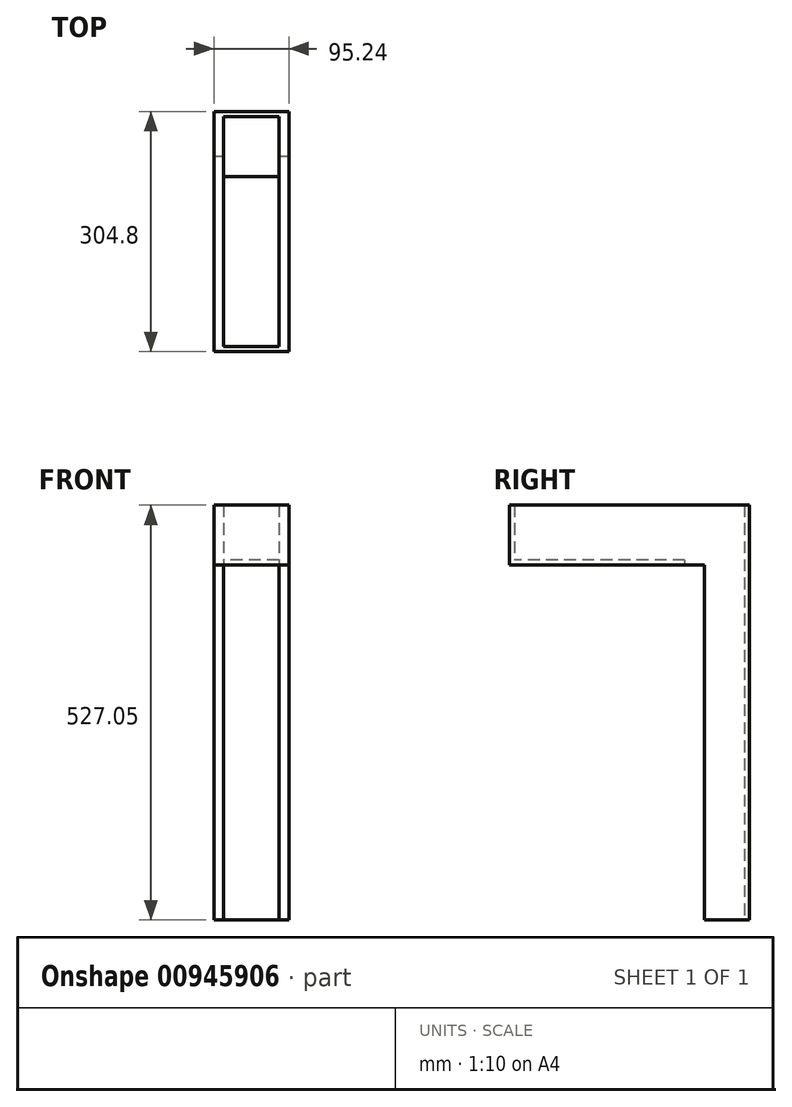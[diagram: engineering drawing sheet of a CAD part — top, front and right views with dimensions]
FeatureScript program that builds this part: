
annotation { "Feature Type Name" : "Feature", "Feature Type Description" : "" }
export const myFeature = defineFeature(function(context is Context, id is Id, definition is map)
    precondition{}
    {
        {
            var Q0;
            Q0=qCreatedBy(makeId("Top.planeOp"),FACE);
            var sketch = newSketch(context, id + "F0", { "sketchPlane" : qUnion([Q0])});
            skLineSegment(sketch, "E0.bottom", {"start": v(47.62, 152.4) * mm, "end": v(-47.63, 152.4) * mm});
            skLineSegment(sketch, "E0.top", {"start": v(47.63, -152.4) * mm, "end": v(-47.62, -152.4) * mm});
            skLineSegment(sketch, "E0.left", {"start": v(47.62, 152.4) * mm, "end": v(47.63, -152.4) * mm});
            skLineSegment(sketch, "E0.right", {"start": v(-47.63, 152.4) * mm, "end": v(-47.62, -152.4) * mm});
            skPoint(sketch, "E0.middle", {"position": v(0, 0) * mm});
            skLineSegment(sketch, "E1.bottom", {"start": v(34.92, 146.05) * mm, "end": v(-34.93, 146.05) * mm});
            skLineSegment(sketch, "E1.top", {"start": v(34.93, -146.05) * mm, "end": v(-34.92, -146.05) * mm});
            skLineSegment(sketch, "E1.left", {"start": v(34.93, 146.05) * mm, "end": v(34.93, -146.05) * mm});
            skLineSegment(sketch, "E1.right", {"start": v(-34.93, 146.05) * mm, "end": v(-34.93, -146.05) * mm});
            skSolve(sketch);
        }
        {
            var Q0;
            Q0=makeQuery(id+"F0.imprint","IMPRINT",FACE,{"disambiguationData":[TD([[makeQuery(id+"F0.imprint","IMPRINT",EDGE,{"derivedFrom":sQuery(id+"F0.wireOp",EDGE,"E0.bottom")}),1.0]])]});
            extrude(context, id + "F1", {"entities" : qUnion([Q0]), "depth" : 69.85 * mm, "offsetDistance" : 25.4 * mm});
        }
        {
            var Q0;
            Q0=makeQuery(id+"F0.imprint","IMPRINT",FACE,{"disambiguationData":[TD([[makeQuery(id+"F0.imprint","IMPRINT",EDGE,{"derivedFrom":sQuery(id+"F0.wireOp",EDGE,"E0.bottom")}),1.0]])]});
            var Q1;
            Q1=makeQuery(id+"F0.imprint","IMPRINT",FACE,{"disambiguationData":[TD([[makeQuery(id+"F0.imprint","IMPRINT",EDGE,{"derivedFrom":sQuery(id+"F0.wireOp",EDGE,"E1.bottom")}),1.0]])]});
            extrude(context, id + "F2", {"entities" : qUnion([Q0, Q1]), "operationType" : NewBodyOperationType.ADD, "oppositeDirection" : true, "depth" : 6.35 * mm, "offsetDistance" : 25.4 * mm});
        }
        {
            var Q0;
            Q0=makeQuery(id+"F2.opExtrude","CAP_FACE",FACE,{"disambiguationData":[OSD([sQuery(id+"F0.wireOp",EDGE,"E0.bottom"),sQuery(id+"F0.wireOp",EDGE,"E0.top"),sQuery(id+"F0.wireOp",EDGE,"E0.left"),sQuery(id+"F0.wireOp",EDGE,"E0.right")])],"isStart":false});
            var sketch = newSketch(context, id + "F3", { "sketchPlane" : qUnion([Q0])});
            skLineSegment(sketch, "E2.bottom", {"start": v(34.92, -146.05) * mm, "end": v(-34.93, -146.05) * mm});
            skLineSegment(sketch, "E2.top", {"start": v(34.92, -69.85) * mm, "end": v(-34.93, -69.85) * mm});
            skLineSegment(sketch, "E2.left", {"start": v(34.92, -146.05) * mm, "end": v(34.93, -69.85) * mm});
            skLineSegment(sketch, "E2.right", {"start": v(-34.93, -146.05) * mm, "end": v(-34.93, -69.85) * mm});
            skSolve(sketch);
        }
        {
            var Q0;
            Q0=makeQuery(id+"F3.imprint","IMPRINT",FACE,{"disambiguationData":[TD([[makeQuery(id+"F3.imprint","IMPRINT",EDGE,{"derivedFrom":sQuery(id+"F3.wireOp",EDGE,"E2.bottom")}),-1.0]])]});
            extrude(context, id + "F4", {"entities" : qUnion([Q0]), "operationType" : NewBodyOperationType.REMOVE, "oppositeDirection" : true, "depth" : 6.35 * mm, "offsetDistance" : 25.4 * mm});
        }
        {
            var Q0;
            Q0=makeQuery(id+"F2.opExtrude","CAP_FACE",FACE,{"disambiguationData":[OSD([sQuery(id+"F0.wireOp",EDGE,"E0.bottom"),sQuery(id+"F0.wireOp",EDGE,"E0.top"),sQuery(id+"F0.wireOp",EDGE,"E0.left"),sQuery(id+"F0.wireOp",EDGE,"E0.right")])],"isStart":false});
            var sketch = newSketch(context, id + "F5", { "sketchPlane" : qUnion([Q0])});
            skLineSegment(sketch, "E3.bottom", {"start": v(47.62, -152.4) * mm, "end": v(-47.63, -152.4) * mm});
            skLineSegment(sketch, "E3.top", {"start": v(47.62, -95.25) * mm, "end": v(34.92, -95.25) * mm});
            skLineSegment(sketch, "E3.left", {"start": v(47.62, -152.4) * mm, "end": v(47.62, -95.25) * mm});
            skLineSegment(sketch, "E3.right", {"start": v(-47.63, -152.4) * mm, "end": v(-47.63, -95.25) * mm});
            skLineSegment(sketch, "E4.bottom", {"start": v(34.92, -146.05) * mm, "end": v(-34.93, -146.05) * mm});
            skLineSegment(sketch, "E4.left", {"start": v(34.92, -146.05) * mm, "end": v(34.92, -95.25) * mm});
            skLineSegment(sketch, "E4.right", {"start": v(-34.93, -146.05) * mm, "end": v(-34.93, -95.25) * mm});
            skLineSegment(sketch, "E5.trimOffspring", {"start": v(-34.93, -95.25) * mm, "end": v(-47.63, -95.25) * mm});
            skSolve(sketch);
        }
        {
            var Q0;
            Q0=makeQuery(id+"F5.imprint","IMPRINT",FACE,{"disambiguationData":[TD([[makeQuery(id+"F5.imprint","IMPRINT",EDGE,{"derivedFrom":sQuery(id+"F5.wireOp",EDGE,"E3.bottom")}),-1.0]])]});
            extrude(context, id + "F6", {"entities" : qUnion([Q0]), "operationType" : NewBodyOperationType.ADD, "depth" : 450.85 * mm, "offsetDistance" : 25.4 * mm});
        }
    });
